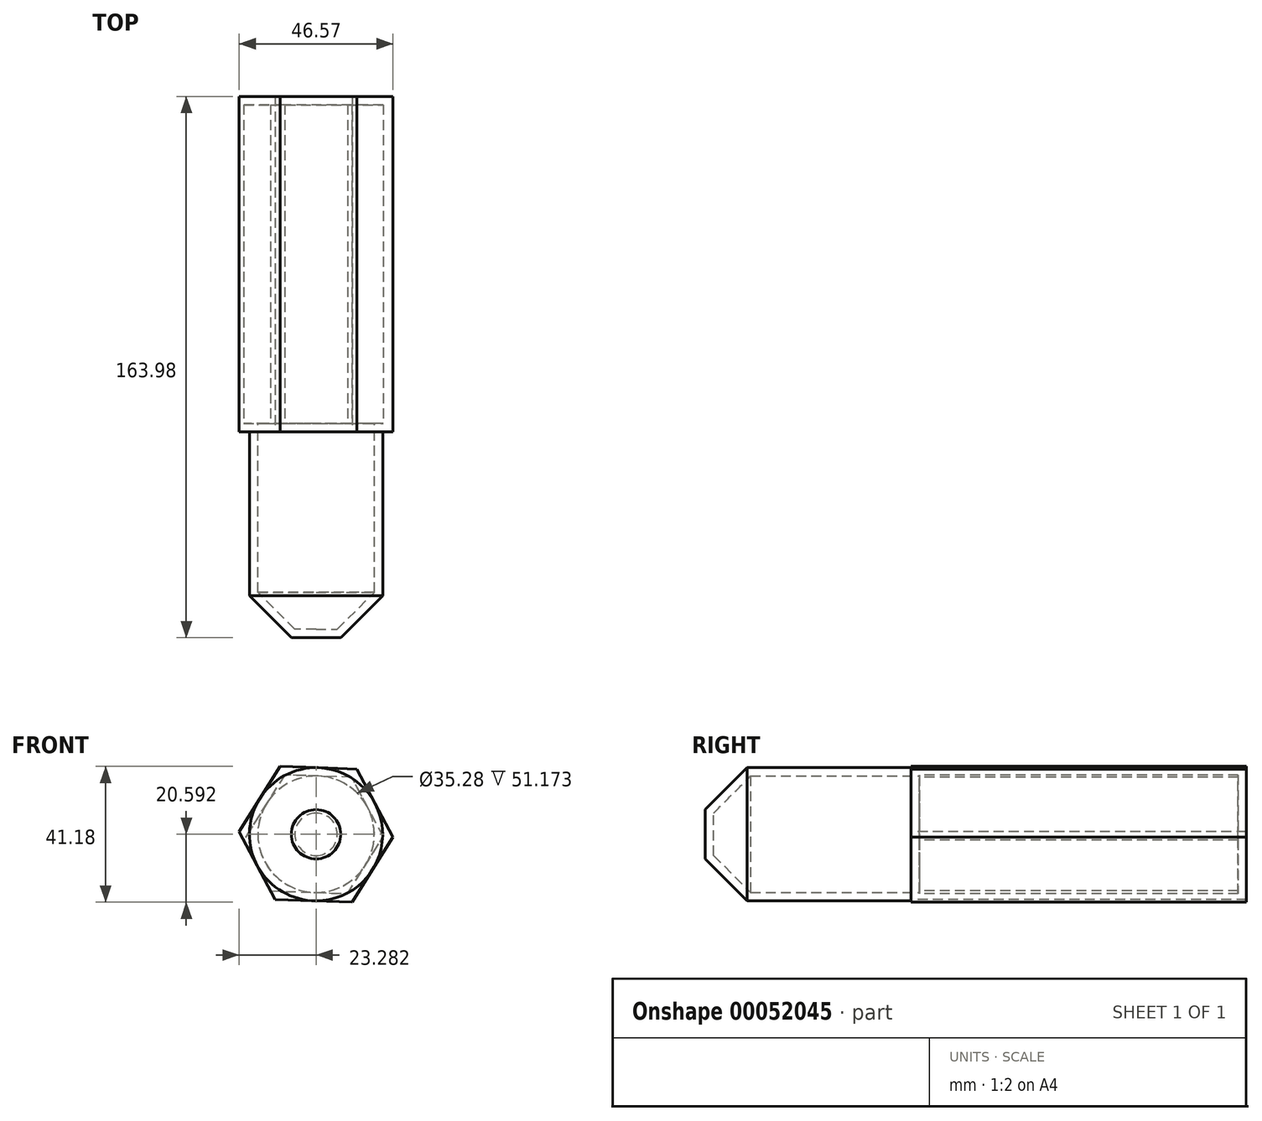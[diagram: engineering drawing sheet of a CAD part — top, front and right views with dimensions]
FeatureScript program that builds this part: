
annotation { "Feature Type Name" : "Feature", "Feature Type Description" : "" }
export const myFeature = defineFeature(function(context is Context, id is Id, definition is map)
    precondition{}
    {
        {
            var Q0;
            Q0=qCreatedBy(makeId("Front.planeOp"),FACE);
            var sketch = newSketch(context, id + "F0", { "sketchPlane" : qUnion([Q0])});
            skCircle(sketch, "E0", {"center": v(-122.2, 38.22) * mm, "radius": 20.18 * mm});
            skSolve(sketch);
        }
        {
            var Q0;
            Q0=makeQuery(id+"F0.imprint","IMPRINT",FACE,{"disambiguationData":[TD([[makeQuery(id+"F0.imprint","IMPRINT",EDGE,{"derivedFrom":sQuery(id+"F0.wireOp",EDGE,"E0")}),1.0]])]});
            extrude(context, id + "F1", {"entities" : qUnion([Q0]), "depth" : 62.38 * mm});
        }
        {
            var Q0;
            Q0=makeQuery(id+"F1.opExtrude","CAP_FACE",FACE,{"disambiguationData":[OSD([sQuery(id+"F0.wireOp",EDGE,"E0")])],"isStart":false});
            chamfer(context, id + "F2", {"entities" : qUnion([Q0]), "width" : 12.7 * mm, "tangentPropagation" : true});
        }
        {
            var Q0;
            Q0=makeQuery(id+"F1.opExtrude","CAP_FACE",FACE,{"disambiguationData":[OSD([sQuery(id+"F0.wireOp",EDGE,"E0")])],"isStart":true});
            var sketch = newSketch(context, id + "F3", { "sketchPlane" : qUnion([Q0])});
            skCircle(sketch, "E1.cCircle", {"center": v(122.2, 38.22) * mm, "radius": 20.18 * mm, "construction": true});
            skLineSegment(sketch, "E1.0", {"start": v(145.48, 39.07) * mm, "end": v(134.58, 18.48) * mm});
            skLineSegment(sketch, "E1.1", {"start": v(134.58, 18.48) * mm, "end": v(111.29, 17.63) * mm});
            skLineSegment(sketch, "E1.2", {"start": v(111.29, 17.63) * mm, "end": v(98.91, 37.37) * mm});
            skLineSegment(sketch, "E1.3", {"start": v(98.91, 37.37) * mm, "end": v(109.82, 57.96) * mm});
            skLineSegment(sketch, "E1.4", {"start": v(109.82, 57.96) * mm, "end": v(133.1, 58.81) * mm});
            skLineSegment(sketch, "E1.5", {"start": v(133.1, 58.81) * mm, "end": v(145.48, 39.07) * mm});
            skPoint(sketch, "E1.0.midPoint", {"position": v(140.03, 28.78) * mm});
            skSolve(sketch);
        }
        {
            var Q0;
            Q0 = qSketchRegion(id + "F3", true);
            extrude(context, id + "F4", {"entities" : qUnion([Q0]), "operationType" : NewBodyOperationType.ADD, "depth" : 101.6 * mm});
        }
        {
            var Q0;
            Q0=makeQuery(id+"F4.opExtrude","SWEPT_FACE",FACE,{"disambiguationData":[OSD([sQuery(id+"F3.wireOp",EDGE,"E1.0")])]});
            shell(context, id + "F5", {"entities" : qUnion([Q0]), "thickness" : 2.54 * mm});
        }
    });
